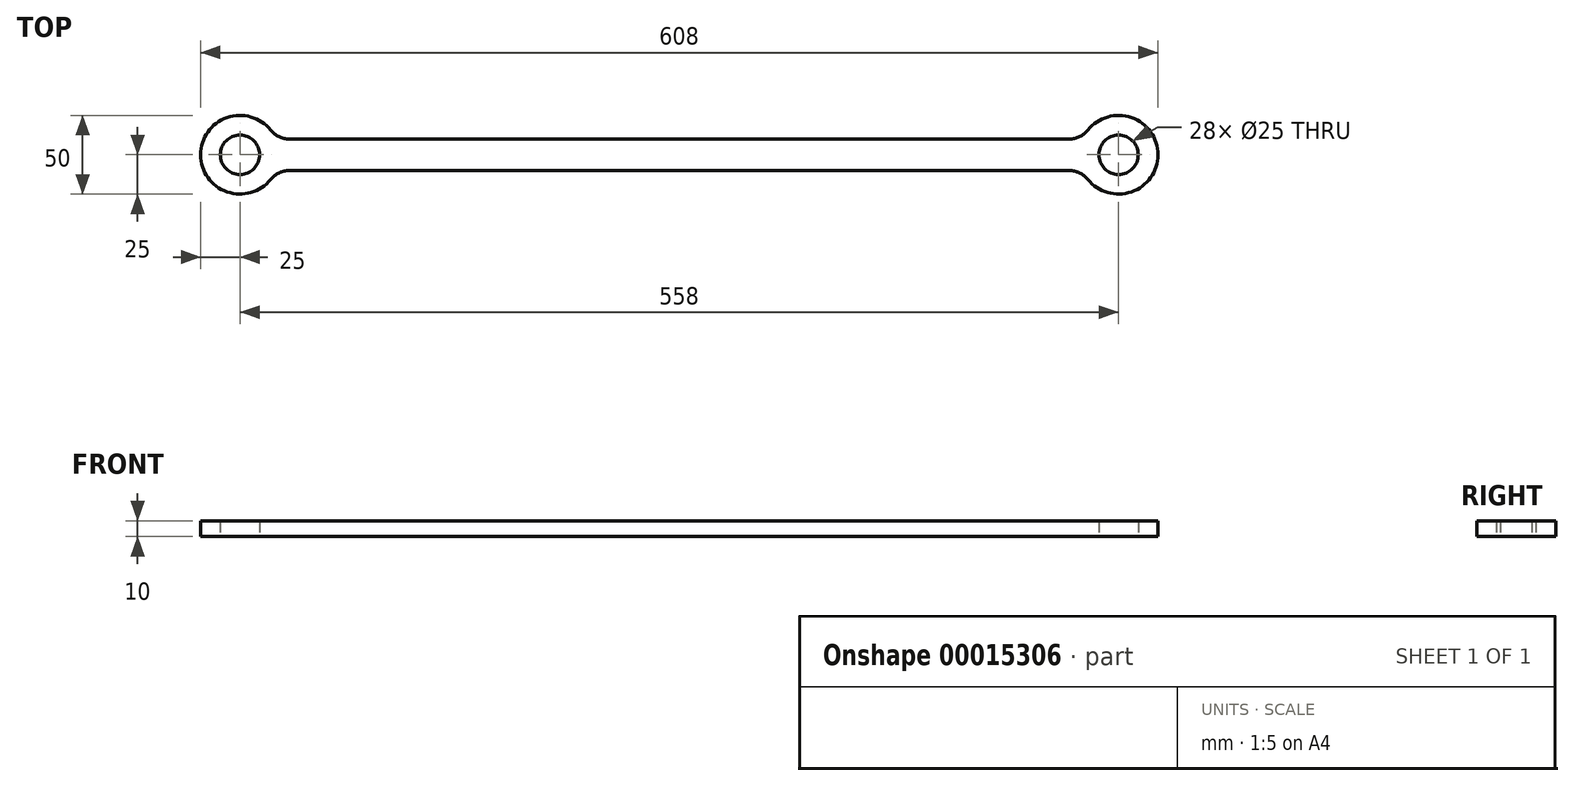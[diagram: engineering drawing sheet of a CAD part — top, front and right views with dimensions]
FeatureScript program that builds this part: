
annotation { "Feature Type Name" : "Feature", "Feature Type Description" : "" }
export const myFeature = defineFeature(function(context is Context, id is Id, definition is map)
    precondition{}
    {
        {
            var Q0;
            Q0=qCreatedBy(makeId("Top.planeOp"),FACE);
            var sketch = newSketch(context, id + "F0", { "sketchPlane" : qUnion([Q0])});
            skArc(sketch, "E0", {"start": v(19.52, 15.63) * mm, "mid": v(-25, 0) * mm, "end": v(19.52, -15.63) * mm});
            skArc(sketch, "E1", {"start": v(538.48, -15.63) * mm, "mid": v(583, 0) * mm, "end": v(538.48, 15.63) * mm});
            skLineSegment(sketch, "E2", {"start": v(31.22, 10) * mm, "end": v(526.78, 10) * mm});
            skLineSegment(sketch, "E3", {"start": v(0, 0) * mm, "end": v(558, 0) * mm, "construction": true});
            skLineSegment(sketch, "E4.MirrorCS", {"start": v(31.22, -10) * mm, "end": v(526.78, -10) * mm});
            skPoint(sketch, "E5.visualSharp", {"position": v(22.91, 10) * mm});
            skArc(sketch, "E5.filletArc", {"start": v(19.52, 15.62) * mm, "mid": v(24.73, 11.48) * mm, "end": v(31.22, 10) * mm});
            skPoint(sketch, "E6.visualSharp", {"position": v(22.91, -10) * mm});
            skArc(sketch, "E6.filletArc", {"start": v(31.22, -10) * mm, "mid": v(24.73, -11.48) * mm, "end": v(19.52, -15.62) * mm});
            skPoint(sketch, "E7.visualSharp", {"position": v(535.09, -10) * mm});
            skArc(sketch, "E7.filletArc", {"start": v(538.48, -15.62) * mm, "mid": v(533.27, -11.48) * mm, "end": v(526.78, -10) * mm});
            skPoint(sketch, "E8.visualSharp", {"position": v(535.09, 10) * mm});
            skArc(sketch, "E8.filletArc", {"start": v(526.78, 10) * mm, "mid": v(533.27, 11.48) * mm, "end": v(538.48, 15.62) * mm});
            skCircle(sketch, "E9", {"center": v(0, 0) * mm, "radius": 12.5 * mm});
            skCircle(sketch, "E10", {"center": v(558, 0) * mm, "radius": 12.5 * mm});
            skSolve(sketch);
        }
        {
            var Q0;
            Q0=qSketchRegion(id+"F0",true);
            extrude(context, id + "F1", {"entities" : qUnion([Q0]), "depth" : 10 * mm});
        }
    });
